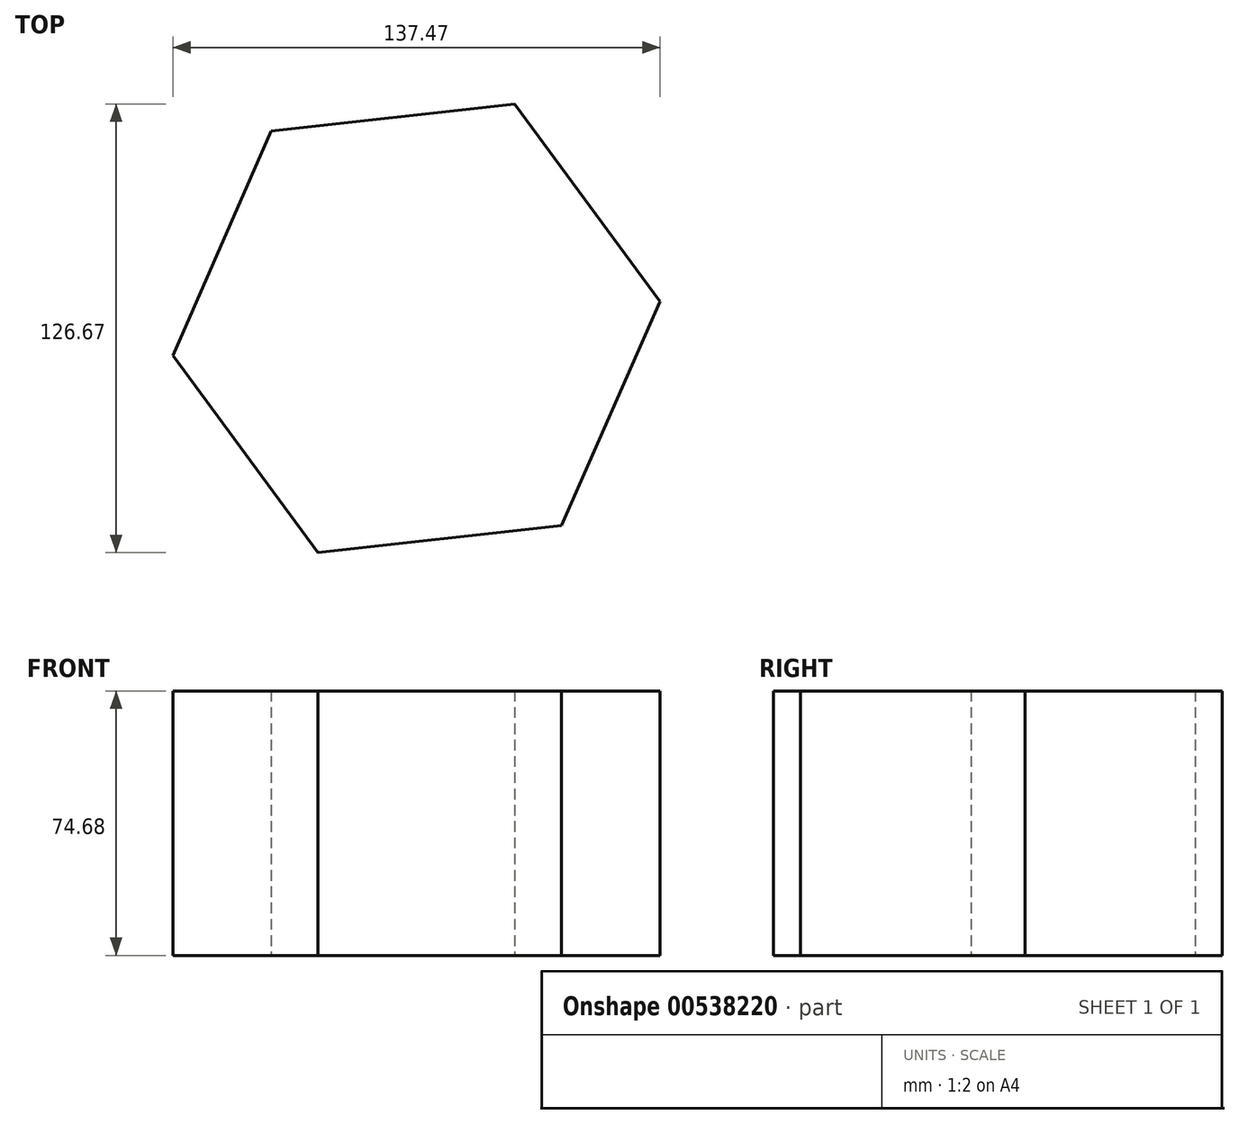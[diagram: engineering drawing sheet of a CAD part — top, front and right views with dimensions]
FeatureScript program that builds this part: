
annotation { "Feature Type Name" : "Feature", "Feature Type Description" : "" }
export const myFeature = defineFeature(function(context is Context, id is Id, definition is map)
    precondition{}
    {
        {
            var Q0;
            Q0=qCreatedBy(makeId("Top.planeOp"),FACE);
            var sketch = newSketch(context, id + "F0", { "sketchPlane" : qUnion([Q0])});
            skCircle(sketch, "E0.cCircle", {"center": v(-121.9, -122.82) * mm, "radius": 59.9 * mm, "construction": true});
            skLineSegment(sketch, "E0.0", {"start": v(-53.17, -115.2) * mm, "end": v(-80.94, -178.54) * mm});
            skLineSegment(sketch, "E0.1", {"start": v(-80.94, -178.54) * mm, "end": v(-149.68, -186.16) * mm});
            skLineSegment(sketch, "E0.2", {"start": v(-149.68, -186.16) * mm, "end": v(-190.64, -130.44) * mm});
            skLineSegment(sketch, "E0.3", {"start": v(-190.64, -130.44) * mm, "end": v(-162.87, -67.1) * mm});
            skLineSegment(sketch, "E0.4", {"start": v(-162.87, -67.1) * mm, "end": v(-94.14, -59.49) * mm});
            skLineSegment(sketch, "E0.5", {"start": v(-94.14, -59.49) * mm, "end": v(-53.17, -115.2) * mm});
            skPoint(sketch, "E0.0.midPoint", {"position": v(-67.06, -146.87) * mm});
            skSolve(sketch);
        }
        {
            var Q0;
            Q0 = qSketchRegion(id + "F0", true);
            extrude(context, id + "F1", {"entities" : qUnion([Q0]), "depth" : 74.68 * mm, "offsetDistance" : 25.4 * mm});
        }
    });
